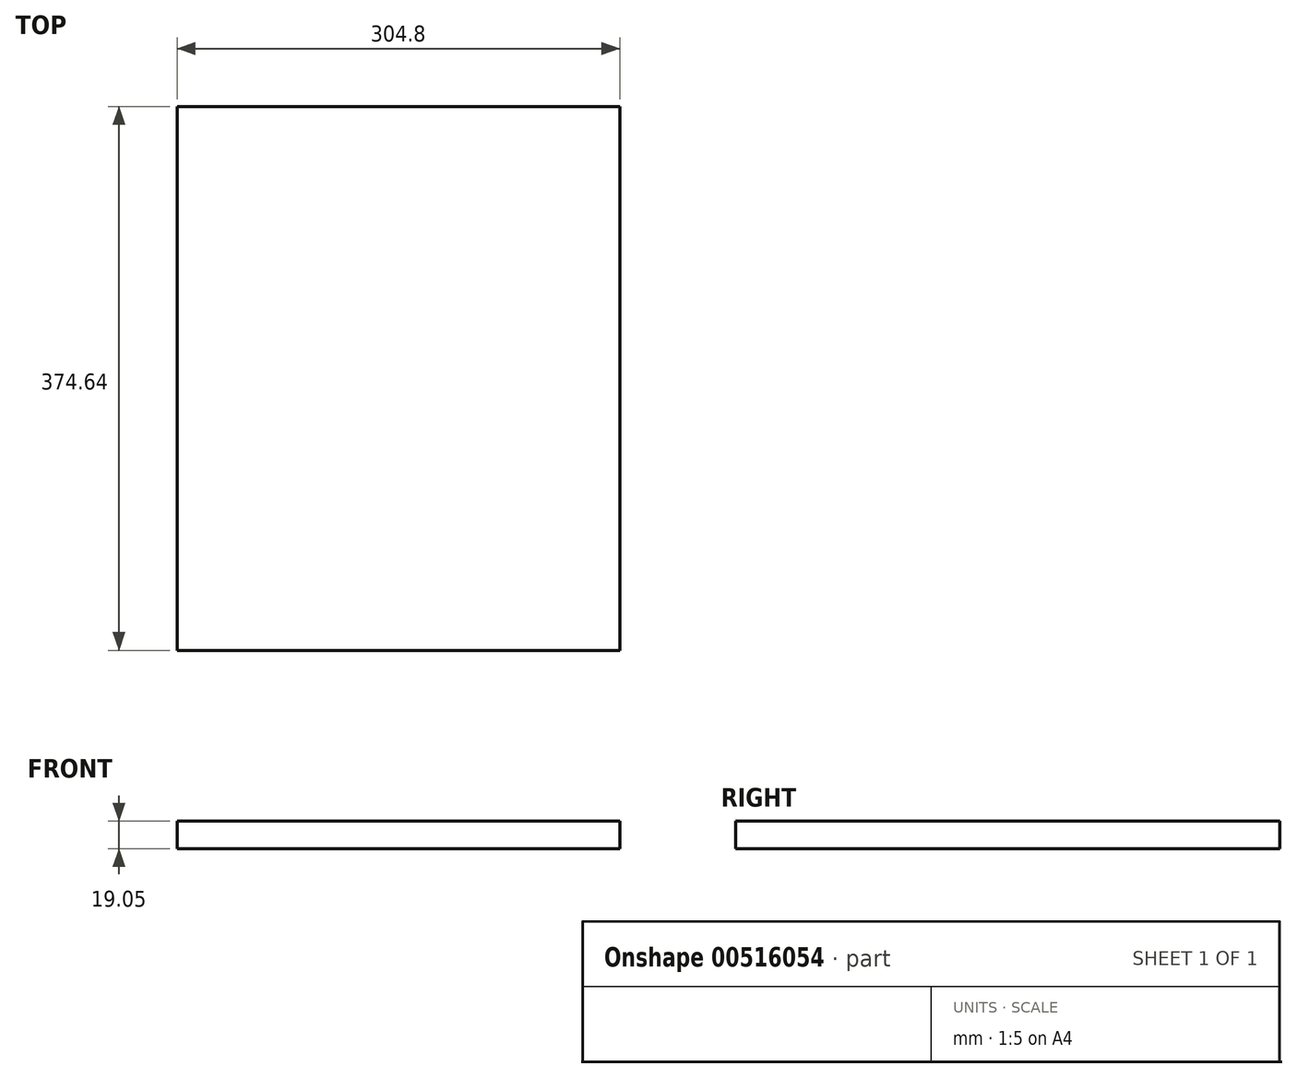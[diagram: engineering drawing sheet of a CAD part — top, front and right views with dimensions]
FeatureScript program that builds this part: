
annotation { "Feature Type Name" : "Feature", "Feature Type Description" : "" }
export const myFeature = defineFeature(function(context is Context, id is Id, definition is map)
    precondition{}
    {
        {
            var Q0;
            Q0=qCreatedBy(makeId("Top.planeOp"),FACE);
            var sketch = newSketch(context, id + "F0", { "sketchPlane" : qUnion([Q0])});
            skLineSegment(sketch, "E0.bottom", {"start": v(152.4, -187.32) * mm, "end": v(-152.4, -187.33) * mm});
            skLineSegment(sketch, "E0.top", {"start": v(152.4, 187.33) * mm, "end": v(-152.4, 187.32) * mm});
            skLineSegment(sketch, "E0.left", {"start": v(152.4, -187.33) * mm, "end": v(152.4, 187.33) * mm});
            skLineSegment(sketch, "E0.right", {"start": v(-152.4, -187.33) * mm, "end": v(-152.4, 187.33) * mm});
            skPoint(sketch, "E0.middle", {"position": v(0, 0) * mm});
            skSolve(sketch);
        }
        {
            var Q0;
            Q0=makeQuery(id+"F0.imprint","IMPRINT",FACE,{"disambiguationData":[TD([[makeQuery(id+"F0.imprint","IMPRINT",EDGE,{"derivedFrom":sQuery(id+"F0.wireOp",EDGE,"E0.bottom")}),-1.0]])]});
            extrude(context, id + "F1", {"entities" : qUnion([Q0]), "depth" : 19.05 * mm, "offsetDistance" : 25.4 * mm});
        }
    });
